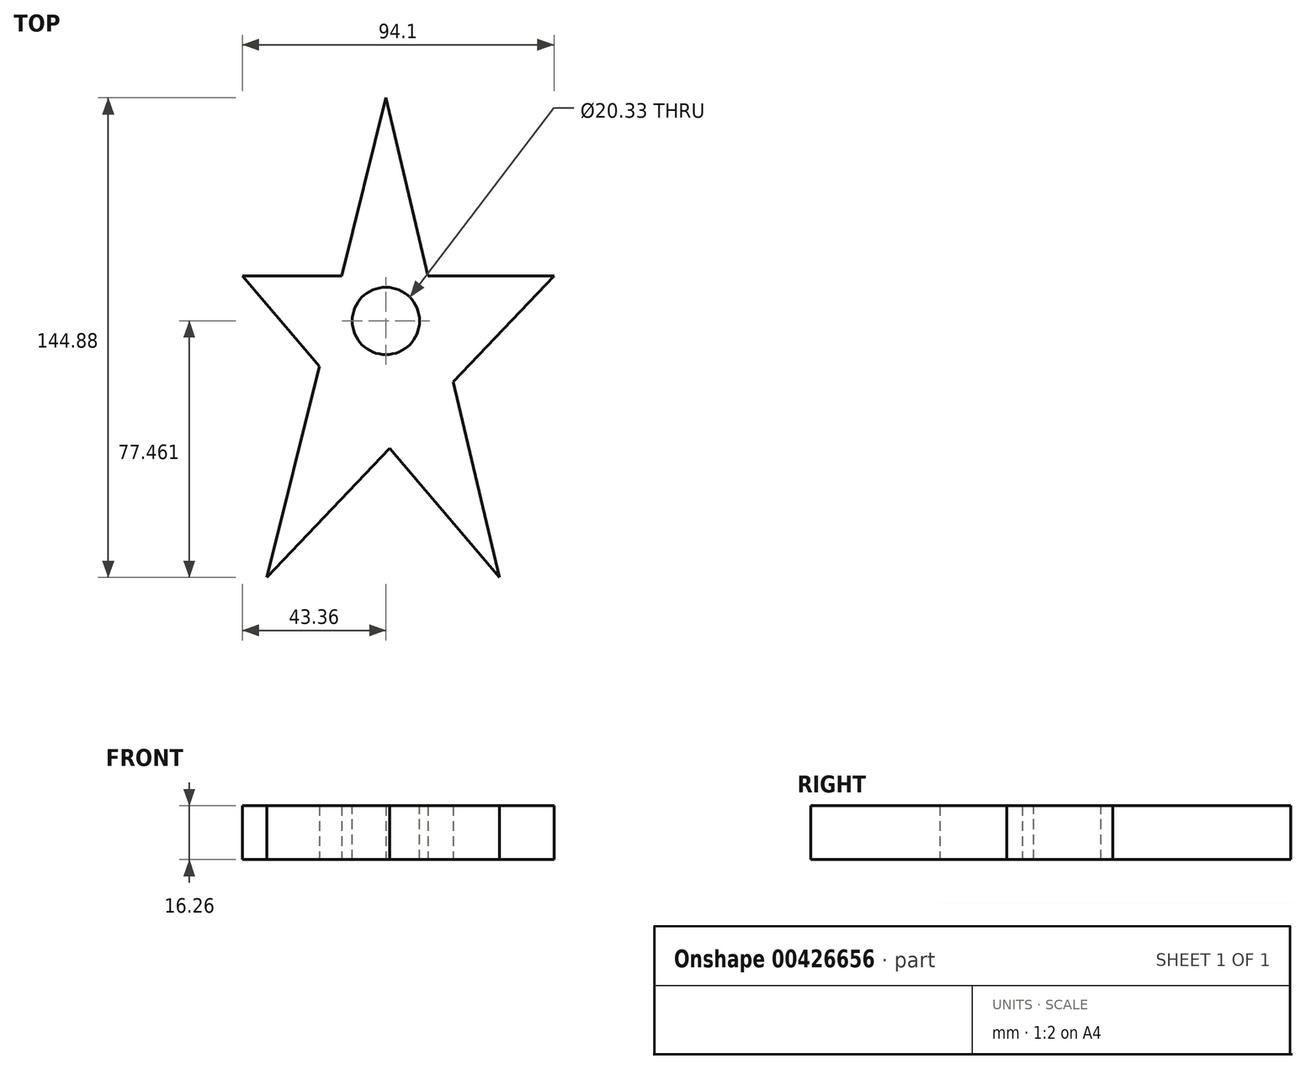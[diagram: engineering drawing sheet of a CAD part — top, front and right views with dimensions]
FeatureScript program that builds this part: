
annotation { "Feature Type Name" : "Feature", "Feature Type Description" : "" }
export const myFeature = defineFeature(function(context is Context, id is Id, definition is map)
    precondition{}
    {
        {
            var Q0;
            Q0=qCreatedBy(makeId("Top.planeOp"),FACE);
            var sketch = newSketch(context, id + "F0", { "sketchPlane" : qUnion([Q0])});
            skLineSegment(sketch, "E0", {"start": v(-43.36, 39.58) * mm, "end": v(50.74, 39.58) * mm});
            skLineSegment(sketch, "E1", {"start": v(50.74, 39.58) * mm, "end": v(-35.9, -51.53) * mm});
            skLineSegment(sketch, "E2", {"start": v(-35.9, -51.53) * mm, "end": v(0, 93.35) * mm});
            skLineSegment(sketch, "E3", {"start": v(0, 93.35) * mm, "end": v(34.3, -51.53) * mm});
            skLineSegment(sketch, "E4", {"start": v(34.3, -51.53) * mm, "end": v(-43.36, 39.58) * mm});
            skSolve(sketch);
        }
        {
            var Q0;
            Q0 = qSketchRegion(id + "F0", true);
            extrude(context, id + "F1", {"entities" : qUnion([Q0]), "depth" : 16.26 * mm});
        }
        {
            var Q0;
            Q0=makeQuery(id+"F1.opExtrude","CAP_FACE",FACE,{"disambiguationData":[OSD([sQuery(id+"F0.wireOp",EDGE,"E0"),sQuery(id+"F0.wireOp",EDGE,"E1"),sQuery(id+"F0.wireOp",EDGE,"E2"),sQuery(id+"F0.wireOp",EDGE,"E3"),sQuery(id+"F0.wireOp",EDGE,"E4")])],"isStart":false});
            var sketch = newSketch(context, id + "F2", { "sketchPlane" : qUnion([Q0])});
            skCircle(sketch, "E5", {"center": v(0, 25.93) * mm, "radius": 10.17 * mm});
            skPoint(sketch, "E5.centerSnap0", {"position": v(-31.72, 25.93) * mm});
            skSolve(sketch);
        }
        {
            var Q0;
            Q0 = qSketchRegion(id + "F2", true);
            extrude(context, id + "F3", {"entities" : qUnion([Q0]), "operationType" : NewBodyOperationType.REMOVE, "oppositeDirection" : true, "depth" : 25.4 * mm});
        }
    });
